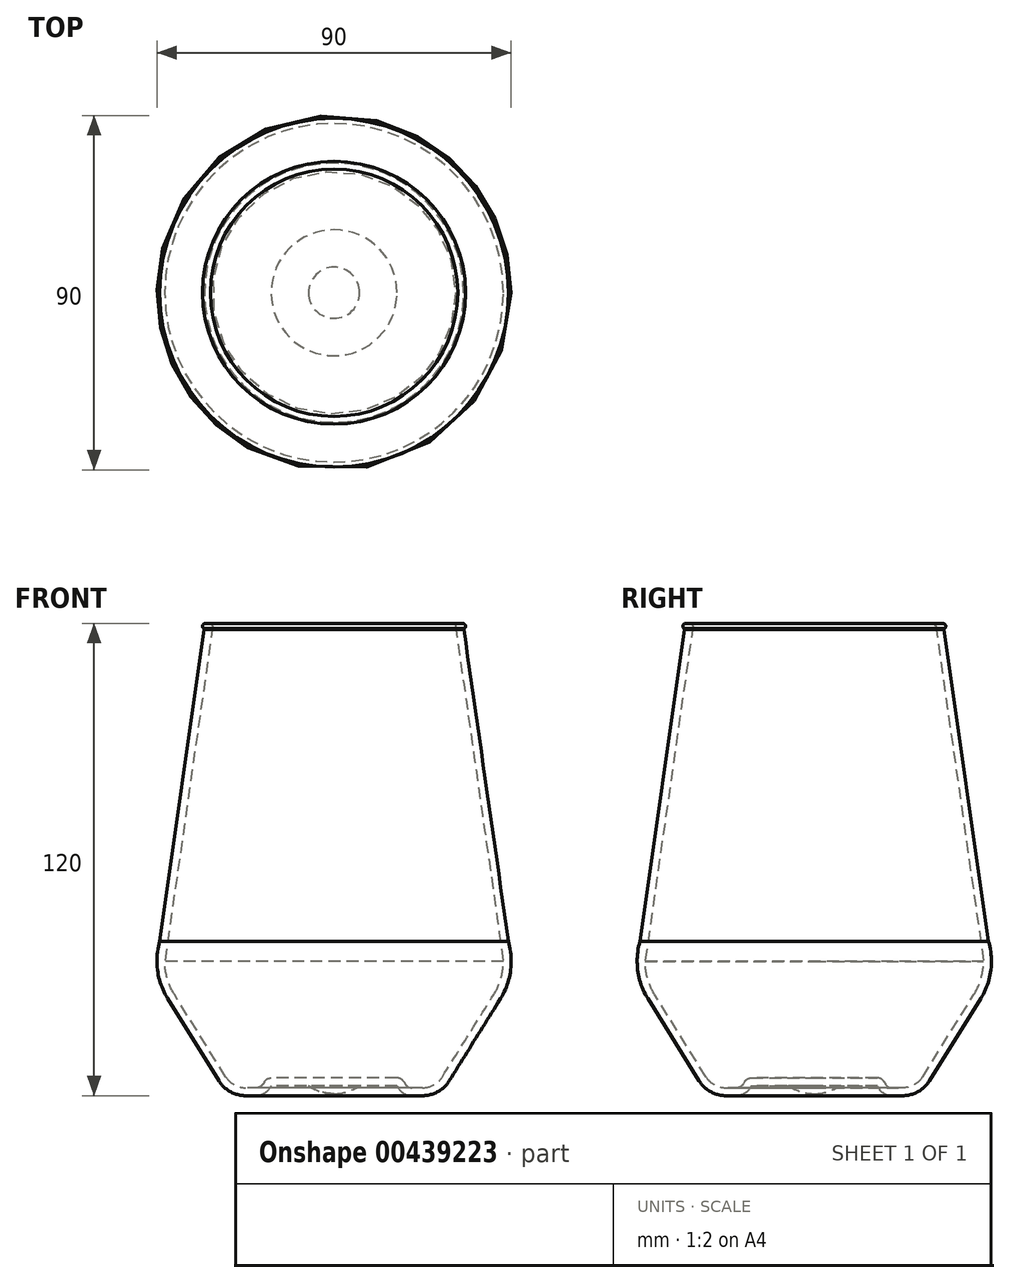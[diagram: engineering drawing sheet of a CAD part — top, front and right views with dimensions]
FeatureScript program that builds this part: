
annotation { "Feature Type Name" : "Feature", "Feature Type Description" : "" }
export const myFeature = defineFeature(function(context is Context, id is Id, definition is map)
    precondition{}
    {
        {
            var Q0;
            Q0=qCreatedBy(makeId("Front.planeOp"),FACE);
            var sketch = newSketch(context, id + "F0", { "sketchPlane" : qUnion([Q0])});
            skArc(sketch, "E0", {"start": v(-43.77, -19.66) * mm, "mid": v(-43.27, -27.56) * mm, "end": v(-39.44, -34.48) * mm});
            skArc(sketch, "E1", {"start": v(39.44, -34.48) * mm, "mid": v(43.27, -27.56) * mm, "end": v(43.77, -19.66) * mm});
            skLineSegment(sketch, "E2", {"start": v(43.77, -19.66) * mm, "end": v(32.97, 48) * mm});
            skLineSegment(sketch, "E3", {"start": v(-32.97, 48) * mm, "end": v(-43.77, -19.66) * mm});
            skLineSegment(sketch, "E4", {"start": v(-39.44, -34.48) * mm, "end": v(-28.43, -46.82) * mm});
            skLineSegment(sketch, "E5", {"start": v(28.43, -46.82) * mm, "end": v(39.44, -34.48) * mm});
            skArc(sketch, "E6", {"start": v(-32.6, 49.5) * mm, "mid": v(-33.19, 49.03) * mm, "end": v(-32.84, 48.35) * mm});
            skArc(sketch, "E7", {"start": v(32.84, 48.35) * mm, "mid": v(33.19, 49.03) * mm, "end": v(32.6, 49.5) * mm});
            skArc(sketch, "E8", {"start": v(32.97, 48) * mm, "mid": v(32.9, 48.18) * mm, "end": v(32.84, 48.35) * mm});
            skArc(sketch, "E9", {"start": v(-32.84, 48.35) * mm, "mid": v(-32.9, 48.18) * mm, "end": v(-32.97, 48) * mm});
            skArc(sketch, "E10", {"start": v(-28.43, -46.82) * mm, "mid": v(-25.73, -48.8) * mm, "end": v(-22.46, -49.5) * mm});
            skArc(sketch, "E11", {"start": v(22.46, -49.5) * mm, "mid": v(25.73, -48.8) * mm, "end": v(28.43, -46.82) * mm});
            skLineSegment(sketch, "E12", {"start": v(-32.97, 48) * mm, "end": v(32.97, 48) * mm});
            skLineSegment(sketch, "E13", {"start": v(-32.84, 48.35) * mm, "end": v(32.84, 48.35) * mm});
            skLineSegment(sketch, "E14", {"start": v(-32.6, 49.5) * mm, "end": v(32.6, 49.5) * mm});
            skLineSegment(sketch, "E15", {"start": v(-22.46, -49.5) * mm, "end": v(22.46, -49.5) * mm});
            skLineSegment(sketch, "E16", {"start": v(-16, -47) * mm, "end": v(16, -47) * mm});
            skArc(sketch, "E17", {"start": v(-19.76, -49.5) * mm, "mid": v(-17.77, -48.97) * mm, "end": v(-16.3, -47.52) * mm});
            skArc(sketch, "E18", {"start": v(16.3, -47.52) * mm, "mid": v(17.77, -48.97) * mm, "end": v(19.76, -49.5) * mm});
            skLineSegment(sketch, "E19", {"start": v(16.3, -47.52) * mm, "end": v(16, -47) * mm});
            skLineSegment(sketch, "E20", {"start": v(-16, -47) * mm, "end": v(-16.3, -47.52) * mm});
            skArc(sketch, "E21", {"start": v(-6.5, -47) * mm, "mid": v(0, -49) * mm, "end": v(6.5, -47) * mm});
            skSolve(sketch);
        }
        {
            var Q0;
            Q0=qCreatedBy(makeId("Front.planeOp"),FACE);
            var sketch = newSketch(context, id + "F1", { "sketchPlane" : qUnion([Q0])});
            skArc(sketch, "E22.0", {"start": v(-32.84, 48.35) * mm, "mid": v(-32.9, 48.18) * mm, "end": v(-32.97, 48) * mm});
            skLineSegment(sketch, "E23.0", {"start": v(-32.84, 48.35) * mm, "end": v(32.84, 48.35) * mm});
            skLineSegment(sketch, "E24.0", {"start": v(-32.97, 48) * mm, "end": v(-43.77, -19.66) * mm});
            skLineSegment(sketch, "E25.0", {"start": v(-16, -47) * mm, "end": v(16, -47) * mm});
            skArc(sketch, "E26.0", {"start": v(-6.5, -47) * mm, "mid": v(0, -49) * mm, "end": v(6.5, -47) * mm});
            skLineSegment(sketch, "E27.0", {"start": v(-16, -47) * mm, "end": v(-16.3, -47.52) * mm});
            skArc(sketch, "E28.0", {"start": v(-19.76, -49.5) * mm, "mid": v(-17.77, -48.97) * mm, "end": v(-16.3, -47.52) * mm});
            skLineSegment(sketch, "E29.0", {"start": v(-22.46, -49.5) * mm, "end": v(22.46, -49.5) * mm});
            skArc(sketch, "E30.0", {"start": v(-28.43, -46.82) * mm, "mid": v(-25.73, -48.8) * mm, "end": v(-22.46, -49.5) * mm});
            skLineSegment(sketch, "E31.0", {"start": v(-39.44, -34.48) * mm, "end": v(-28.43, -46.82) * mm});
            skArc(sketch, "E32.0", {"start": v(-43.77, -19.66) * mm, "mid": v(-43.27, -27.56) * mm, "end": v(-39.44, -34.48) * mm});
            skLineSegment(sketch, "E33.0", {"start": v(-32.6, 49.5) * mm, "end": v(32.6, 49.5) * mm});
            skArc(sketch, "E34.0", {"start": v(-32.6, 49.5) * mm, "mid": v(-33.19, 49.03) * mm, "end": v(-32.84, 48.35) * mm});
            skSolve(sketch);
        }
        {
            var Q0;
            Q0=qCreatedBy(makeId("Front.planeOp"),FACE);
            var sketch = newSketch(context, id + "F2", { "sketchPlane" : qUnion([Q0])});
            skLineSegment(sketch, "E35.0", {"start": v(-32.6, 49.5) * mm, "end": v(32.6, 49.5) * mm});
            skArc(sketch, "E36", {"start": v(-32.65, 49.5) * mm, "mid": v(-33.18, 49.28) * mm, "end": v(-33.4, 48.75) * mm});
            skArc(sketch, "E37", {"start": v(-33.4, 48.75) * mm, "mid": v(-33.26, 48.37) * mm, "end": v(-32.91, 48.16) * mm});
            skLineSegment(sketch, "E38", {"start": v(-32.6, 49.5) * mm, "end": v(-32.65, 49.5) * mm});
            skArc(sketch, "E39.0", {"start": v(-32.91, 48.16) * mm, "mid": v(-32.94, 48.08) * mm, "end": v(-32.97, 48) * mm});
            skPoint(sketch, "E40.orphan", {"position": v(-32.84, 48.35) * mm});
            skSolve(sketch);
        }
        {
            var Q0;
            Q0=qCreatedBy(makeId("Front.planeOp"),FACE);
            var sketch = newSketch(context, id + "F3", { "sketchPlane" : qUnion([Q0])});
            skArc(sketch, "E41.0", {"start": v(-32.65, 49.5) * mm, "mid": v(-33.18, 49.28) * mm, "end": v(-33.4, 48.75) * mm});
            skArc(sketch, "E42.0", {"start": v(-33.4, 48.75) * mm, "mid": v(-33.26, 48.37) * mm, "end": v(-32.91, 48.16) * mm});
            skArc(sketch, "E43.0", {"start": v(-32.91, 48.16) * mm, "mid": v(-32.94, 48.08) * mm, "end": v(-32.97, 48) * mm});
            skLineSegment(sketch, "E44", {"start": v(-32.97, 48) * mm, "end": v(-43.84, -32.76) * mm});
            skLineSegment(sketch, "E45", {"start": v(-41.9, -43.61) * mm, "end": v(-35.17, -56.26) * mm});
            skLineSegment(sketch, "E46", {"start": v(-28.1, -60.5) * mm, "end": v(-19.76, -60.5) * mm});
            skPoint(sketch, "E47.visualSharp", {"position": v(-44.61, -38.5) * mm});
            skArc(sketch, "E47.filletArc", {"start": v(-43.84, -32.76) * mm, "mid": v(-43.72, -38.34) * mm, "end": v(-41.9, -43.61) * mm});
            skPoint(sketch, "E48.0", {"position": v(0, -47) * mm});
            skLineSegment(sketch, "E49", {"start": v(0, -47) * mm, "end": v(0, 55.6) * mm});
            skLineSegment(sketch, "E50", {"start": v(-16, -58) * mm, "end": v(-6.5, -58) * mm});
            skLineSegment(sketch, "E51", {"start": v(-16, -58) * mm, "end": v(-16.3, -58.52) * mm});
            skArc(sketch, "E52.filletArc", {"start": v(-19.76, -60.5) * mm, "mid": v(-17.77, -59.97) * mm, "end": v(-16.3, -58.52) * mm});
            skArc(sketch, "E53", {"start": v(-6.5, -58) * mm, "mid": v(-3.4, -59.49) * mm, "end": v(0, -60) * mm});
            skPoint(sketch, "E54.start.orphan", {"position": v(0, -58) * mm});
            skPoint(sketch, "E55.end.orphan", {"position": v(6.5, -58) * mm});
            skPoint(sketch, "E56.visualSharp", {"position": v(-32.91, -60.5) * mm});
            skArc(sketch, "E56.filletArc", {"start": v(-35.17, -56.26) * mm, "mid": v(-32.23, -59.36) * mm, "end": v(-28.1, -60.5) * mm});
            skSolve(sketch);
        }
        {
            var Q0;
            Q0=qCreatedBy(makeId("Front.planeOp"),FACE);
            var sketch = newSketch(context, id + "F4", { "sketchPlane" : qUnion([Q0])});
            skLineSegment(sketch, "E57.0", {"start": v(-16, -58) * mm, "end": v(-6.5, -58) * mm});
            skLineSegment(sketch, "E58.0", {"start": v(-16, -58) * mm, "end": v(-16.3, -58.52) * mm});
            skArc(sketch, "E59.0", {"start": v(-19.76, -60.5) * mm, "mid": v(-17.77, -59.97) * mm, "end": v(-16.3, -58.52) * mm});
            skLineSegment(sketch, "E60.0", {"start": v(-28.1, -60.5) * mm, "end": v(-19.76, -60.5) * mm});
            skArc(sketch, "E61.0", {"start": v(-35.17, -56.26) * mm, "mid": v(-32.23, -59.36) * mm, "end": v(-28.1, -60.5) * mm});
            skLineSegment(sketch, "E62.0", {"start": v(-41.9, -43.61) * mm, "end": v(-35.17, -56.26) * mm});
            skArc(sketch, "E63.0", {"start": v(-43.84, -32.76) * mm, "mid": v(-43.72, -38.34) * mm, "end": v(-41.9, -43.61) * mm});
            skLineSegment(sketch, "E64.0", {"start": v(-32.97, 48) * mm, "end": v(-43.84, -32.76) * mm});
            skArc(sketch, "E65.0", {"start": v(-32.91, 48.16) * mm, "mid": v(-32.94, 48.08) * mm, "end": v(-32.97, 48) * mm});
            skArc(sketch, "E66.0", {"start": v(-33.4, 48.75) * mm, "mid": v(-33.26, 48.37) * mm, "end": v(-32.91, 48.16) * mm});
            skArc(sketch, "E67.0", {"start": v(-32.65, 49.5) * mm, "mid": v(-33.18, 49.28) * mm, "end": v(-33.4, 48.75) * mm});
            skLineSegment(sketch, "E68", {"start": v(-32.65, 49.5) * mm, "end": v(-31.44, 49.5) * mm});
            skLineSegment(sketch, "E69.0", {"start": v(-30.84, 48.82) * mm, "end": v(-41.86, -33.03) * mm});
            skLineSegment(sketch, "E70.0", {"start": v(-40.13, -42.67) * mm, "end": v(-33.4, -55.32) * mm});
            skLineSegment(sketch, "E71.0", {"start": v(-28.1, -58.5) * mm, "end": v(-19.76, -58.5) * mm});
            skLineSegment(sketch, "E72.0", {"start": v(-17.73, -57) * mm, "end": v(-18.03, -57.5) * mm});
            skLineSegment(sketch, "E73", {"start": v(0, -56) * mm, "end": v(0, -60) * mm});
            skArc(sketch, "E74.0", {"start": v(-6.5, -58) * mm, "mid": v(-3.4, -59.49) * mm, "end": v(0, -60) * mm});
            skArc(sketch, "E75.filletArc", {"start": v(-30.84, 48.82) * mm, "mid": v(-30.98, 49.3) * mm, "end": v(-31.44, 49.5) * mm});
            skArc(sketch, "E76.filletArc", {"start": v(-41.86, -33.03) * mm, "mid": v(-41.75, -37.98) * mm, "end": v(-40.13, -42.67) * mm});
            skArc(sketch, "E77.filletArc", {"start": v(-33.4, -55.32) * mm, "mid": v(-31.2, -57.64) * mm, "end": v(-28.1, -58.5) * mm});
            skArc(sketch, "E78.filletArc", {"start": v(-19.76, -58.5) * mm, "mid": v(-18.76, -58.23) * mm, "end": v(-18.03, -57.5) * mm});
            skLineSegment(sketch, "E79", {"start": v(-16, -56) * mm, "end": v(0, -56) * mm});
            skArc(sketch, "E80", {"start": v(-16, -56) * mm, "mid": v(-17, -56.27) * mm, "end": v(-17.73, -57) * mm});
            skSolve(sketch);
        }
        {
            var Q0;
            Q0=makeQuery(id+"F4.imprint","IMPRINT",FACE,{"disambiguationData":[TD([[makeQuery(id+"F4.imprint","IMPRINT",EDGE,{"derivedFrom":sQuery(id+"F4.wireOp",EDGE,"E57.0")}),1.0]])]});
            var Q1;
            Q1=sQuery(id+"F4.wireOp",EDGE,"E73");
            revolve(context, id + "F5", {"entities" : qUnion([Q0]), "axis" : qUnion([Q1]), "revolveType" : RevolveType.FULL});
        }
        {
            var Q0;
            Q0=qCreatedBy(makeId("Front.planeOp"),FACE);
            var sketch = newSketch(context, id + "F6", { "sketchPlane" : qUnion([Q0])});
            skArc(sketch, "E81.0", {"start": v(-41.86, -33.03) * mm, "mid": v(-41.75, -37.98) * mm, "end": v(-40.13, -42.67) * mm});
            skLineSegment(sketch, "E82.0", {"start": v(-30.84, 48.82) * mm, "end": v(-41.86, -33.03) * mm});
            skLineSegment(sketch, "E83.0", {"start": v(-40.13, -42.67) * mm, "end": v(-33.4, -55.32) * mm});
            skArc(sketch, "E84.0", {"start": v(-33.4, -55.32) * mm, "mid": v(-31.2, -57.64) * mm, "end": v(-28.1, -58.5) * mm});
            skLineSegment(sketch, "E85.0", {"start": v(-28.1, -58.5) * mm, "end": v(-19.76, -58.5) * mm});
            skArc(sketch, "E86.0", {"start": v(-19.76, -58.5) * mm, "mid": v(-18.76, -58.23) * mm, "end": v(-18.03, -57.5) * mm});
            skLineSegment(sketch, "E87.0", {"start": v(-17.73, -57) * mm, "end": v(-18.03, -57.5) * mm});
            skArc(sketch, "E88.0", {"start": v(-16, -56) * mm, "mid": v(-17, -56.27) * mm, "end": v(-17.73, -57) * mm});
            skLineSegment(sketch, "E89.0", {"start": v(-16, -56) * mm, "end": v(0, -56) * mm});
            skArc(sketch, "E90.0", {"start": v(-30.84, 48.82) * mm, "mid": v(-30.98, 49.3) * mm, "end": v(-31.44, 49.5) * mm});
            skLineSegment(sketch, "E91", {"start": v(-31.44, 49.5) * mm, "end": v(0, 49.5) * mm});
            skLineSegment(sketch, "E92", {"start": v(0, 49.5) * mm, "end": v(0, -56) * mm});
            skSolve(sketch);
        }
        {
            var Q0;
            Q0=makeQuery(id+"F6.imprint","IMPRINT",FACE,{"disambiguationData":[TD([[makeQuery(id+"F6.imprint","IMPRINT",EDGE,{"derivedFrom":sQuery(id+"F6.wireOp",EDGE,"E81.0")}),1.0]])]});
            var Q1;
            Q1=sQuery(id+"F6.wireOp",EDGE,"E92");
            revolve(context, id + "F7", {"entities" : qUnion([Q0]), "axis" : qUnion([Q1]), "revolveType" : RevolveType.FULL});
        }
        {
            var Q0;
            Q0=makeQuery(id+"F7.opRevolve","SWEPT_FACE",FACE,{"disambiguationData":[OSD([sQuery(id+"F6.wireOp",EDGE,"E91")])]});
            var sketch = newSketch(context, id + "F8", { "sketchPlane" : qUnion([Q0])});
            skCircle(sketch, "E93", {"center": v(0, 0) * mm, "radius": 107.31 * mm});
            skSolve(sketch);
        }
        {
            var Q0;
            Q0 = qSketchRegion(id + "F8", true);
            extrude(context, id + "F9", {"entities" : qUnion([Q0]), "operationType" : NewBodyOperationType.REMOVE, "oppositeDirection" : true, "depth" : 36 * mm});
        }
        {
            var Q0;
            Q0=qCreatedBy(makeId("Front.planeOp"),FACE);
            var sketch = newSketch(context, id + "F10", { "sketchPlane" : qUnion([Q0])});
            skArc(sketch, "E94.0", {"start": v(-33.4, 48.75) * mm, "mid": v(-33.26, 48.37) * mm, "end": v(-32.91, 48.16) * mm});
            skArc(sketch, "E95.0", {"start": v(-32.65, 49.5) * mm, "mid": v(-33.18, 49.28) * mm, "end": v(-33.4, 48.75) * mm});
            skArc(sketch, "E96.0", {"start": v(-32.91, 48.16) * mm, "mid": v(-32.94, 48.08) * mm, "end": v(-32.97, 48) * mm});
            skPoint(sketch, "E97.0", {"position": v(-26, -22.5) * mm});
            skPoint(sketch, "E98.0", {"position": v(-22.46, -41.5) * mm});
            skPoint(sketch, "E99.0", {"position": v(-6.5, -47) * mm});
            skPoint(sketch, "E100.0", {"position": v(0, -49) * mm});
            skPoint(sketch, "E101.0", {"position": v(0, -37.44) * mm});
            skPoint(sketch, "E102.0", {"position": v(-16, -47) * mm});
            skPoint(sketch, "E103.0", {"position": v(-19.76, -45.5) * mm});
            skLineSegment(sketch, "E104", {"start": v(-27, -22.36) * mm, "end": v(-27, 6.85) * mm, "construction": true});
            skLineSegment(sketch, "E105", {"start": v(-22.46, -41.5) * mm, "end": v(-22.46, -31.1) * mm, "construction": true});
            skLineSegment(sketch, "E106", {"start": v(-32.97, 48) * mm, "end": v(-44.3, -31.35) * mm});
            skLineSegment(sketch, "E107", {"start": v(-42.27, -45.85) * mm, "end": v(-29.24, -66.73) * mm});
            skPoint(sketch, "E108.visualSharp", {"position": v(-45.6, -40.5) * mm});
            skLineSegment(sketch, "E109", {"start": v(-22.46, -70.5) * mm, "end": v(-19.76, -70.5) * mm});
            skPoint(sketch, "E110.visualSharp", {"position": v(-26.9, -70.5) * mm});
            skArc(sketch, "E110.filletArc", {"start": v(-29.24, -66.73) * mm, "mid": v(-26.34, -69.5) * mm, "end": v(-22.46, -70.5) * mm});
            skArc(sketch, "E111", {"start": v(-44.3, -31.35) * mm, "mid": v(-44.83, -38.81) * mm, "end": v(-42.27, -45.85) * mm});
            skLineSegment(sketch, "E112", {"start": v(-16, -68) * mm, "end": v(-6.5, -68) * mm});
            skLineSegment(sketch, "E113.0", {"start": v(-16, -47) * mm, "end": v(-16.3, -47.52) * mm, "construction": true});
            skLineSegment(sketch, "E114", {"start": v(-16, -68) * mm, "end": v(-16.3, -68.52) * mm});
            skPoint(sketch, "E115.newPointB", {"position": v(0, -70.5) * mm});
            skArc(sketch, "E115.filletArc", {"start": v(-19.76, -70.5) * mm, "mid": v(-17.77, -69.97) * mm, "end": v(-16.3, -68.52) * mm});
            skLineSegment(sketch, "E116.MirrorCS", {"start": v(16, -68) * mm, "end": v(6.5, -68) * mm, "construction": true});
            skArc(sketch, "E117", {"start": v(-6.5, -68) * mm, "mid": v(-3.4, -69.49) * mm, "end": v(0, -70) * mm});
            skLineSegment(sketch, "E118", {"start": v(-6.5, -47) * mm, "end": v(-6.5, -68) * mm, "construction": true});
            skLineSegment(sketch, "E119", {"start": v(0, -70) * mm, "end": v(0, -37.44) * mm, "construction": true});
            skSolve(sketch);
        }
        {
            var Q0;
            Q0=qCreatedBy(makeId("Front.planeOp"),FACE);
            var sketch = newSketch(context, id + "F11", { "sketchPlane" : qUnion([Q0])});
            skLineSegment(sketch, "E120.0", {"start": v(-32.97, 48) * mm, "end": v(-44.3, -31.35) * mm});
            skArc(sketch, "E121.0", {"start": v(-44.3, -31.35) * mm, "mid": v(-44.83, -38.81) * mm, "end": v(-42.27, -45.85) * mm});
            skLineSegment(sketch, "E122.0", {"start": v(-42.27, -45.85) * mm, "end": v(-29.24, -66.73) * mm});
            skArc(sketch, "E123.0", {"start": v(-32.91, 48.16) * mm, "mid": v(-32.94, 48.08) * mm, "end": v(-32.97, 48) * mm});
            skArc(sketch, "E124.0", {"start": v(-33.4, 48.75) * mm, "mid": v(-33.26, 48.37) * mm, "end": v(-32.91, 48.16) * mm});
            skArc(sketch, "E125.0", {"start": v(-32.65, 49.5) * mm, "mid": v(-33.18, 49.28) * mm, "end": v(-33.4, 48.75) * mm});
            skArc(sketch, "E126.0", {"start": v(-29.24, -66.73) * mm, "mid": v(-26.34, -69.5) * mm, "end": v(-22.46, -70.5) * mm});
            skLineSegment(sketch, "E127.0", {"start": v(-22.46, -70.5) * mm, "end": v(-19.76, -70.5) * mm});
            skArc(sketch, "E128.0", {"start": v(-19.76, -70.5) * mm, "mid": v(-17.77, -69.97) * mm, "end": v(-16.3, -68.52) * mm});
            skPoint(sketch, "E129.0", {"position": v(-16.15, -68.26) * mm});
            skLineSegment(sketch, "E130.0", {"start": v(-16, -68) * mm, "end": v(-16.3, -68.52) * mm});
            skLineSegment(sketch, "E131.0", {"start": v(-16, -68) * mm, "end": v(-6.5, -68) * mm});
            skArc(sketch, "E132.0", {"start": v(-6.5, -68) * mm, "mid": v(-3.4, -69.49) * mm, "end": v(0, -70) * mm});
            skLineSegment(sketch, "E133.0", {"start": v(-16, -66) * mm, "end": v(-6.5, -66) * mm});
            skArc(sketch, "E134.0", {"start": v(-19.76, -68.5) * mm, "mid": v(-18.76, -68.24) * mm, "end": v(-18.03, -67.51) * mm});
            skArc(sketch, "E135.0", {"start": v(-27.55, -65.68) * mm, "mid": v(-25.37, -67.75) * mm, "end": v(-22.46, -68.5) * mm});
            skArc(sketch, "E136.0", {"start": v(-43, -36.4) * mm, "mid": v(-42.37, -40.76) * mm, "end": v(-40.58, -44.79) * mm});
            skLineSegment(sketch, "E137.0", {"start": v(-30.83, 48.82) * mm, "end": v(-43, -36.4) * mm});
            skLineSegment(sketch, "E138", {"start": v(-22.46, -68.5) * mm, "end": v(-19.76, -68.5) * mm});
            skLineSegment(sketch, "E139", {"start": v(-18.03, -67.51) * mm, "end": v(-17.73, -66.99) * mm});
            skArc(sketch, "E140.filletArc", {"start": v(-16, -66) * mm, "mid": v(-17, -66.26) * mm, "end": v(-17.73, -66.99) * mm});
            skLineSegment(sketch, "E141", {"start": v(-6.5, -66) * mm, "end": v(0, -66) * mm});
            skLineSegment(sketch, "E142", {"start": v(0, -66) * mm, "end": v(0, -70) * mm});
            skLineSegment(sketch, "E143", {"start": v(-32.65, 49.5) * mm, "end": v(-31.43, 49.5) * mm});
            skArc(sketch, "E144.filletArc", {"start": v(-30.83, 48.82) * mm, "mid": v(-30.97, 49.3) * mm, "end": v(-31.43, 49.5) * mm});
            skLineSegment(sketch, "E145.0", {"start": v(-40.58, -44.79) * mm, "end": v(-27.55, -65.68) * mm});
            skSolve(sketch);
        }
        {
            var Q0;
            Q0=makeQuery(id+"F11.imprint","IMPRINT",FACE,{"disambiguationData":[TD([[makeQuery(id+"F11.imprint","IMPRINT",EDGE,{"derivedFrom":sQuery(id+"F11.wireOp",EDGE,"E120.0")}),1.0]])]});
            var Q1;
            Q1=sQuery(id+"F11.wireOp",EDGE,"E142");
            revolve(context, id + "F12", {"entities" : qUnion([Q0]), "axis" : qUnion([Q1]), "revolveType" : RevolveType.FULL});
        }
        {
            var Q0;
            Q0=qCreatedBy(makeId("Front.planeOp"),FACE);
            var sketch = newSketch(context, id + "F13", { "sketchPlane" : qUnion([Q0])});
            skArc(sketch, "E146.0", {"start": v(-27.55, -65.68) * mm, "mid": v(-25.37, -67.75) * mm, "end": v(-22.46, -68.5) * mm});
            skLineSegment(sketch, "E147.0", {"start": v(-22.46, -68.5) * mm, "end": v(-19.76, -68.5) * mm});
            skArc(sketch, "E148.0", {"start": v(-19.76, -68.5) * mm, "mid": v(-18.76, -68.24) * mm, "end": v(-18.03, -67.51) * mm});
            skLineSegment(sketch, "E149.0", {"start": v(-18.03, -67.51) * mm, "end": v(-17.73, -66.99) * mm});
            skArc(sketch, "E150.0", {"start": v(-16, -66) * mm, "mid": v(-17, -66.26) * mm, "end": v(-17.73, -66.99) * mm});
            skLineSegment(sketch, "E151.0", {"start": v(-16, -66) * mm, "end": v(-6.5, -66) * mm});
            skLineSegment(sketch, "E152.0", {"start": v(-6.5, -66) * mm, "end": v(0, -66) * mm});
            skArc(sketch, "E153.0", {"start": v(-43, -36.4) * mm, "mid": v(-42.37, -40.76) * mm, "end": v(-40.58, -44.79) * mm});
            skLineSegment(sketch, "E154.0", {"start": v(-30.83, 48.82) * mm, "end": v(-43, -36.4) * mm});
            skArc(sketch, "E155.0", {"start": v(-30.83, 48.82) * mm, "mid": v(-30.97, 49.3) * mm, "end": v(-31.43, 49.5) * mm});
            skLineSegment(sketch, "E156", {"start": v(-31.43, 49.5) * mm, "end": v(0, 49.5) * mm});
            skLineSegment(sketch, "E157", {"start": v(0, 49.5) * mm, "end": v(0, -66) * mm});
            skLineSegment(sketch, "E158.0", {"start": v(-40.58, -44.79) * mm, "end": v(-27.55, -65.68) * mm});
            skSolve(sketch);
        }
        {
            var Q0;
            Q0 = qSketchRegion(id + "F13", true);
            var Q1;
            Q1=sQuery(id+"F13.wireOp",EDGE,"E157");
            revolve(context, id + "F14", {"entities" : qUnion([Q0]), "axis" : qUnion([Q1]), "revolveType" : RevolveType.FULL});
        }
        {
            var Q0;
            Q0=makeQuery(id+"F14.opRevolve","SWEPT_FACE",FACE,{"disambiguationData":[OSD([sQuery(id+"F13.wireOp",EDGE,"E156")])]});
            var sketch = newSketch(context, id + "F15", { "sketchPlane" : qUnion([Q0])});
            skCircle(sketch, "E159", {"center": v(0, 0) * mm, "radius": 102.3 * mm});
            skSolve(sketch);
        }
        {
            var Q0;
            Q0=makeQuery(id+"F5.opRevolve","SWEPT_BODY",BODY,{"disambiguationData":[OSD([sQuery(id+"F4.wireOp",EDGE,"E57.0"),sQuery(id+"F4.wireOp",EDGE,"E58.0"),sQuery(id+"F4.wireOp",EDGE,"E59.0"),sQuery(id+"F4.wireOp",EDGE,"E60.0"),sQuery(id+"F4.wireOp",EDGE,"E61.0"),sQuery(id+"F4.wireOp",EDGE,"E62.0"),sQuery(id+"F4.wireOp",EDGE,"E63.0"),sQuery(id+"F4.wireOp",EDGE,"E64.0"),sQuery(id+"F4.wireOp",EDGE,"E65.0"),sQuery(id+"F4.wireOp",EDGE,"E66.0"),sQuery(id+"F4.wireOp",EDGE,"E67.0"),sQuery(id+"F4.wireOp",EDGE,"E68"),sQuery(id+"F4.wireOp",EDGE,"E69.0"),sQuery(id+"F4.wireOp",EDGE,"E70.0"),sQuery(id+"F4.wireOp",EDGE,"E71.0"),sQuery(id+"F4.wireOp",EDGE,"E72.0"),sQuery(id+"F4.wireOp",EDGE,"E73"),sQuery(id+"F4.wireOp",EDGE,"E74.0"),sQuery(id+"F4.wireOp",EDGE,"E75.filletArc"),sQuery(id+"F4.wireOp",EDGE,"E76.filletArc"),sQuery(id+"F4.wireOp",EDGE,"E77.filletArc"),sQuery(id+"F4.wireOp",EDGE,"E78.filletArc"),sQuery(id+"F4.wireOp",EDGE,"E79"),sQuery(id+"F4.wireOp",EDGE,"E80")])]});
            deleteBodies(context, id + "F16", {"entities" : qUnion([Q0])});
        }
        {
            var Q0;
            Q0=makeQuery(id+"F7.opRevolve","SWEPT_BODY",BODY,{"disambiguationData":[OSD([sQuery(id+"F6.wireOp",EDGE,"E81.0"),sQuery(id+"F6.wireOp",EDGE,"E82.0"),sQuery(id+"F6.wireOp",EDGE,"E83.0"),sQuery(id+"F6.wireOp",EDGE,"E84.0"),sQuery(id+"F6.wireOp",EDGE,"E85.0"),sQuery(id+"F6.wireOp",EDGE,"E86.0"),sQuery(id+"F6.wireOp",EDGE,"E87.0"),sQuery(id+"F6.wireOp",EDGE,"E88.0"),sQuery(id+"F6.wireOp",EDGE,"E89.0"),sQuery(id+"F6.wireOp",EDGE,"E90.0"),sQuery(id+"F6.wireOp",EDGE,"E91"),sQuery(id+"F6.wireOp",EDGE,"E92")])]});
            deleteBodies(context, id + "F17", {"entities" : qUnion([Q0])});
        }
    });
